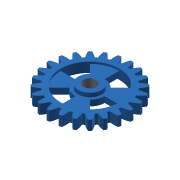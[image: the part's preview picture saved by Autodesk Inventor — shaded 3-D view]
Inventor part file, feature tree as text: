
AUTODESK INVENTOR PART (.ipt)
format: ipt  version: 2020 (Build 240168000, 168)  size: 349,696 bytes
history: native  units: mm (DEFAULTED — no unit token found)
features: sketch x10, extrude x9, plane x4, other x3, pattern_circular x1, mirror x1
ambient origin geometry x8: Origin, YZ Plane, XZ Plane, XY Plane, X Axis, Y Axis, Z Axis, Center Point
bodies: Solid1 (feature_tree)
feature tree (28):
  extrude  "Extrusion1"  Depth=5.0mm TaperAngle=0.0deg
  plane  "Work Plane2"
  plane  "Work Plane8"
  plane  "Work Plane9"
  other  "Spur Gear"
  extrude  "Extrusion5"  Depth=10.0mm TaperAngle=0.0deg
  extrude  "Extrusion6"  Depth=1.308997mm TaperAngle=0.0deg
  pattern_circular  "Circular Pattern1"  Count=3  [1 undecoded]
  extrude  "Extrusion7"  TaperAngle=0.0deg  [1 undecoded]
  plane  "Work Plane11"
  mirror  "Mirror1"
  extrude  "Extrusion9"  Depth=5.0mm TaperAngle=0.0deg
  extrude  "Extrusion10"  TaperAngle=135.0deg  [1 undecoded]
  extrude  "Extrusion11"  Depth=5.0mm TaperAngle=0.0deg
  extrude  "Extrusion12"  Depth=1.0mm TaperAngle=0.0deg
  extrude  "Extrusion13"  [1 undecoded]
  sketch  "Sketch1"  dims[d0=43.066667mm d1=5.0mm d2=0.0mm]
  sketch  "Sketch2"  dims[d3=40.0mm d4=10.0mm d5=0.0mm]
  other  "Srf1"
  sketch  "Sketch9"  dims[d16=30.0mm d17=0.0mm d34=1.308997mm]
  sketch  "Sketch10"  dims[d39=0.0mm]
  sketch  "Sketch11"  dims[d41=0.0mm d43=30.0mm]
  sketch  "Sketch14"  dims[d46=30.0mm d47=0.0mm d48=0.0mm]
  sketch  "Sketch15"  dims[d78=6.1mm d79=5.0mm d80=0.0mm]
  sketch  "Sketch16"  dims[d81=30.0mm d82=135.0deg]
  sketch  "Sketch17"  dims[d83=15.0mm d84=5.0mm d85=0.0mm]
  sketch  "Sketch18"  dims[d86=40.0mm d87=360.0deg d89=1.0mm d90=0.0mm d91=-2.5mm d96=12.0mm d97=2.0mm d98=0.0mm d100=5.0mm d101=0.0mm d102=5.0mm d103=0.0mm d104=6.4mm d105=5.0mm d106=0.0mm d108=5.0mm d109=0.0mm]
  other  "Pitch Diameter"
note: 4 required parameter values undecoded (feature->parameter linkage not recoverable at this tier; creation-order binding heuristic only, values carry confidence <= 0.55)
